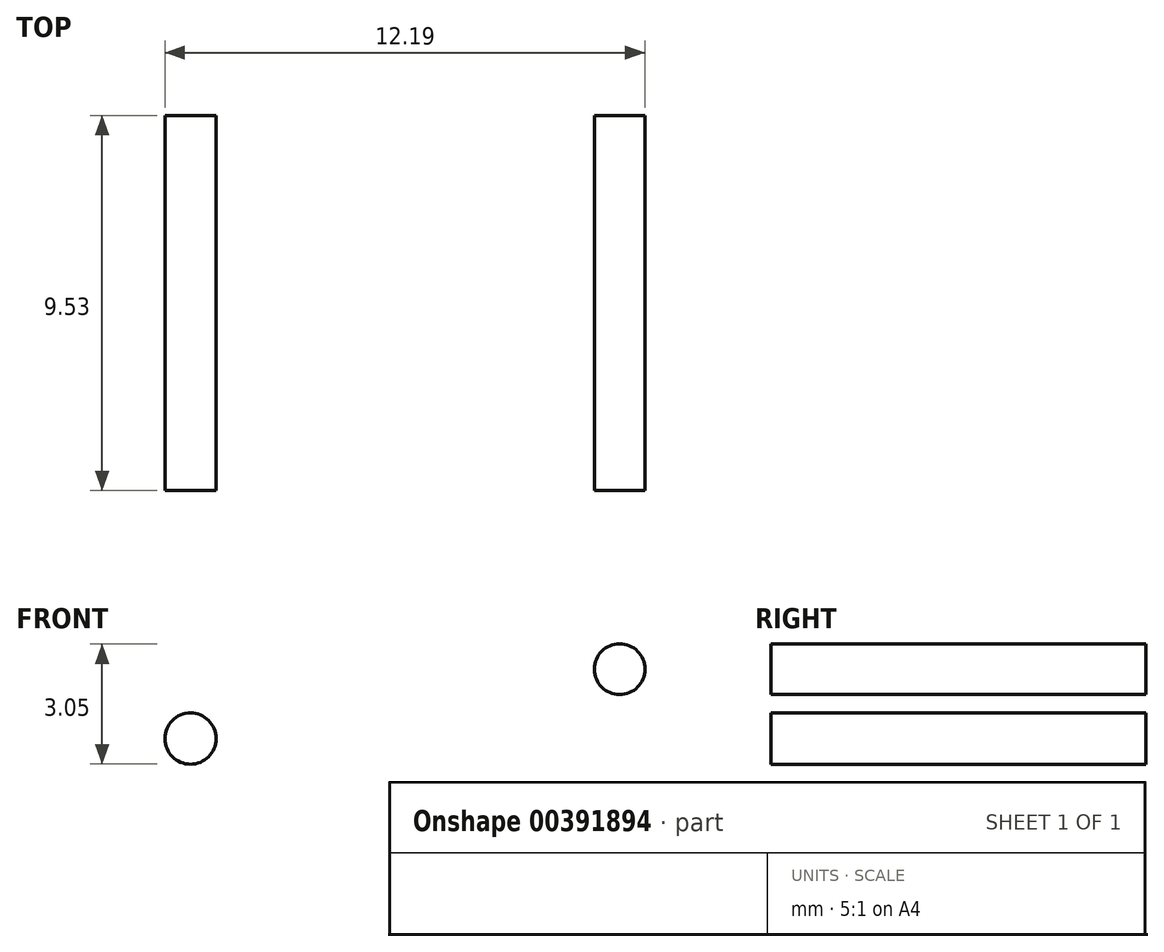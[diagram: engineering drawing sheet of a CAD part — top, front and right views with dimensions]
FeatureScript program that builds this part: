
annotation { "Feature Type Name" : "Feature", "Feature Type Description" : "" }
export const myFeature = defineFeature(function(context is Context, id is Id, definition is map)
    precondition{}
    {
        {
            var Q0;
            Q0=qCreatedBy(makeId("Front.planeOp"),FACE);
            var sketch = newSketch(context, id + "F0", { "sketchPlane" : qUnion([Q0])});
            skCircle(sketch, "E0", {"center": v(-25.97, 39.42) * mm, "radius": 0.65 * mm});
            skCircle(sketch, "E1", {"center": v(-21.57, 39.66) * mm, "radius": 0.64 * mm});
            skCircle(sketch, "E2", {"center": v(-32.47, 37.9) * mm, "radius": 0.65 * mm});
            skSolve(sketch);
        }
        {
            var Q0;
            Q0=makeQuery(id+"F0.imprint","IMPRINT",FACE,{"disambiguationData":[TD([[makeQuery(id+"F0.imprint","IMPRINT",EDGE,{"derivedFrom":sQuery(id+"F0.wireOp",EDGE,"E1")}),1.0]])]});
            var Q1;
            Q1=makeQuery(id+"F0.imprint","IMPRINT",FACE,{"disambiguationData":[TD([[makeQuery(id+"F0.imprint","IMPRINT",EDGE,{"derivedFrom":sQuery(id+"F0.wireOp",EDGE,"E2")}),1.0]])]});
            extrude(context, id + "F1", {"entities" : qUnion([Q0, Q1]), "depth" : 9.52 * mm});
        }
    });
